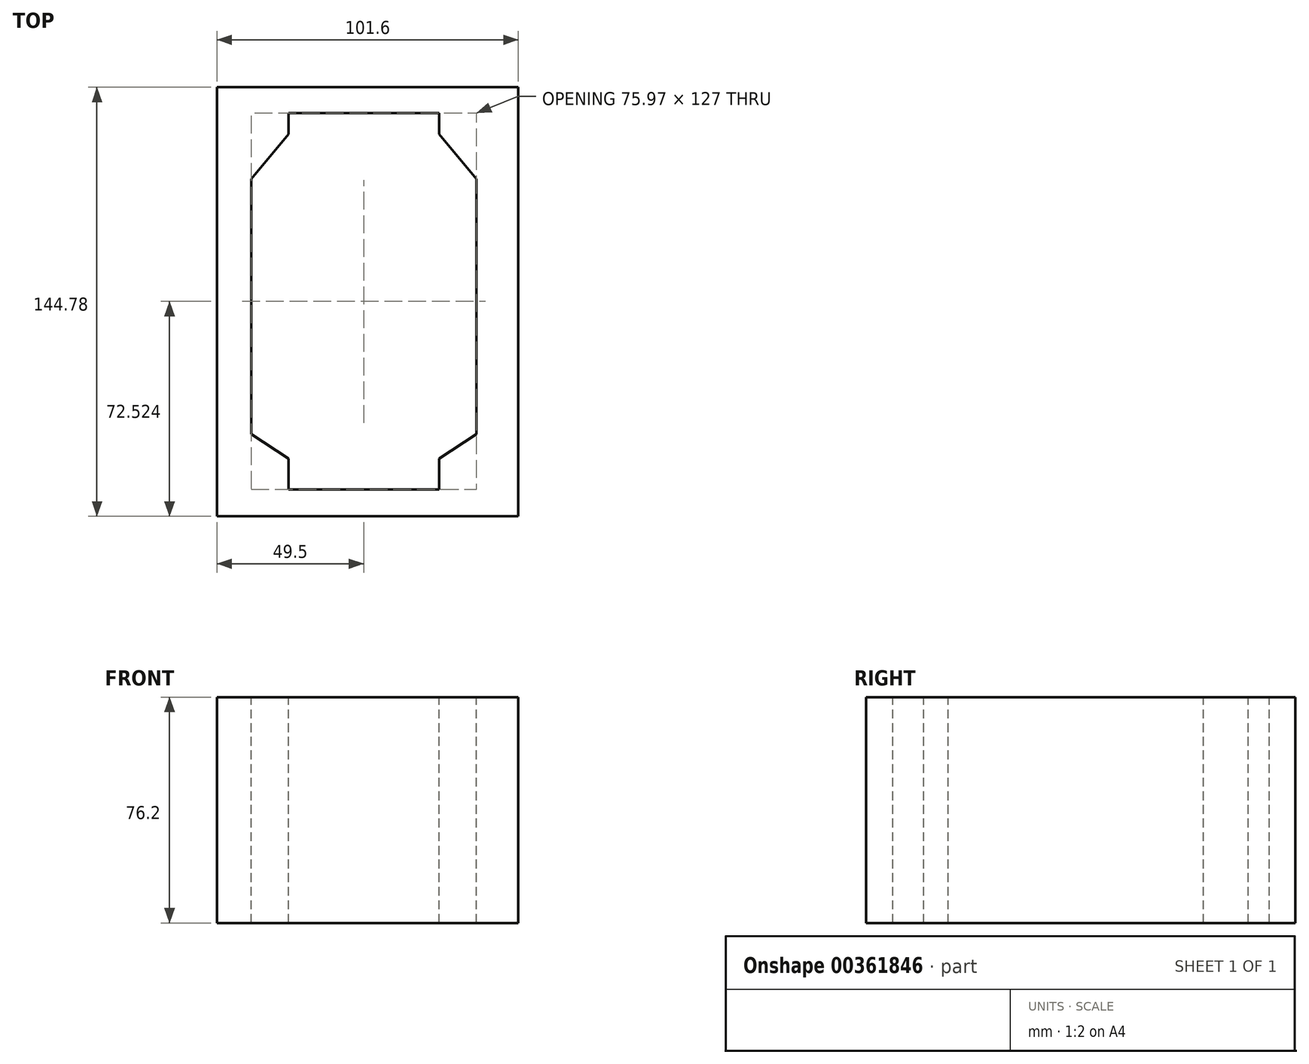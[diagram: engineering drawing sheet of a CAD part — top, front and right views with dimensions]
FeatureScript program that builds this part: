
annotation { "Feature Type Name" : "Feature", "Feature Type Description" : "" }
export const myFeature = defineFeature(function(context is Context, id is Id, definition is map)
    precondition{}
    {
        {
            var Q0;
            Q0=qCreatedBy(makeId("Top.planeOp"),FACE);
            var sketch = newSketch(context, id + "F0", { "sketchPlane" : qUnion([Q0])});
            skLineSegment(sketch, "E0.bottom", {"start": v(-76.93, 91.83) * mm, "end": v(24.67, 91.83) * mm});
            skLineSegment(sketch, "E0.top", {"start": v(-76.93, -52.95) * mm, "end": v(24.67, -52.95) * mm});
            skLineSegment(sketch, "E0.left", {"start": v(-76.93, 91.83) * mm, "end": v(-76.93, -52.95) * mm});
            skLineSegment(sketch, "E0.right", {"start": v(24.67, 91.83) * mm, "end": v(24.67, -52.95) * mm});
            skSolve(sketch);
        }
        {
            var Q0;
            Q0=makeQuery(id+"F0.imprint","IMPRINT",FACE,{"disambiguationData":[TD([[makeQuery(id+"F0.imprint","IMPRINT",EDGE,{"derivedFrom":sQuery(id+"F0.wireOp",EDGE,"E0.bottom")}),-1.0]])]});
            extrude(context, id + "F1", {"entities" : qUnion([Q0]), "depth" : 76.2 * mm});
        }
        {
            var Q0;
            Q0=makeQuery(id+"F1.opExtrude","CAP_FACE",FACE,{"disambiguationData":[OSD([sQuery(id+"F0.wireOp",EDGE,"E0.bottom"),sQuery(id+"F0.wireOp",EDGE,"E0.top"),sQuery(id+"F0.wireOp",EDGE,"E0.left"),sQuery(id+"F0.wireOp",EDGE,"E0.right")])],"isStart":false});
            var sketch = newSketch(context, id + "F2", { "sketchPlane" : qUnion([Q0])});
            skPoint(sketch, "E1.firstSnap0", {"position": v(-26.13, 91.83) * mm});
            skLineSegment(sketch, "E2.bottom", {"start": v(-52.83, 83.07) * mm, "end": v(-2.03, 83.07) * mm});
            skLineSegment(sketch, "E2.top", {"start": v(-52.83, -43.93) * mm, "end": v(-2.03, -43.93) * mm});
            skLineSegment(sketch, "E3", {"start": v(-52.83, 76) * mm, "end": v(-65.42, 60.88) * mm});
            skLineSegment(sketch, "E4", {"start": v(-65.42, 60.88) * mm, "end": v(-65.42, -25.2) * mm});
            skLineSegment(sketch, "E5", {"start": v(-65.42, -25.2) * mm, "end": v(-52.83, -33.42) * mm});
            skLineSegment(sketch, "E6.MirrorCS", {"start": v(10.56, 60.88) * mm, "end": v(10.56, -25.2) * mm});
            skLineSegment(sketch, "E7.MirrorCS", {"start": v(-2.03, 76) * mm, "end": v(10.56, 60.88) * mm});
            skLineSegment(sketch, "E8.MirrorCS", {"start": v(10.56, -25.2) * mm, "end": v(-2.03, -33.42) * mm});
            skLineSegment(sketch, "E9", {"start": v(-52.83, 76) * mm, "end": v(-52.83, 83.07) * mm});
            skLineSegment(sketch, "E10", {"start": v(-2.03, 76) * mm, "end": v(-2.03, 83.07) * mm});
            skLineSegment(sketch, "E11", {"start": v(-2.03, -33.42) * mm, "end": v(-2.03, -43.93) * mm});
            skLineSegment(sketch, "E12", {"start": v(-52.83, -43.93) * mm, "end": v(-52.83, -33.42) * mm});
            skSolve(sketch);
        }
        {
            var Q0;
            Q0=makeQuery(id+"F2.imprint","IMPRINT",FACE,{"disambiguationData":[TD([[makeQuery(id+"F2.imprint","IMPRINT",EDGE,{"derivedFrom":sQuery(id+"F2.wireOp",EDGE,"E2.bottom")}),-1.0]])]});
            extrude(context, id + "F3", {"entities" : qUnion([Q0]), "operationType" : NewBodyOperationType.REMOVE, "oppositeDirection" : true, "depth" : 76.2 * mm});
        }
    });
